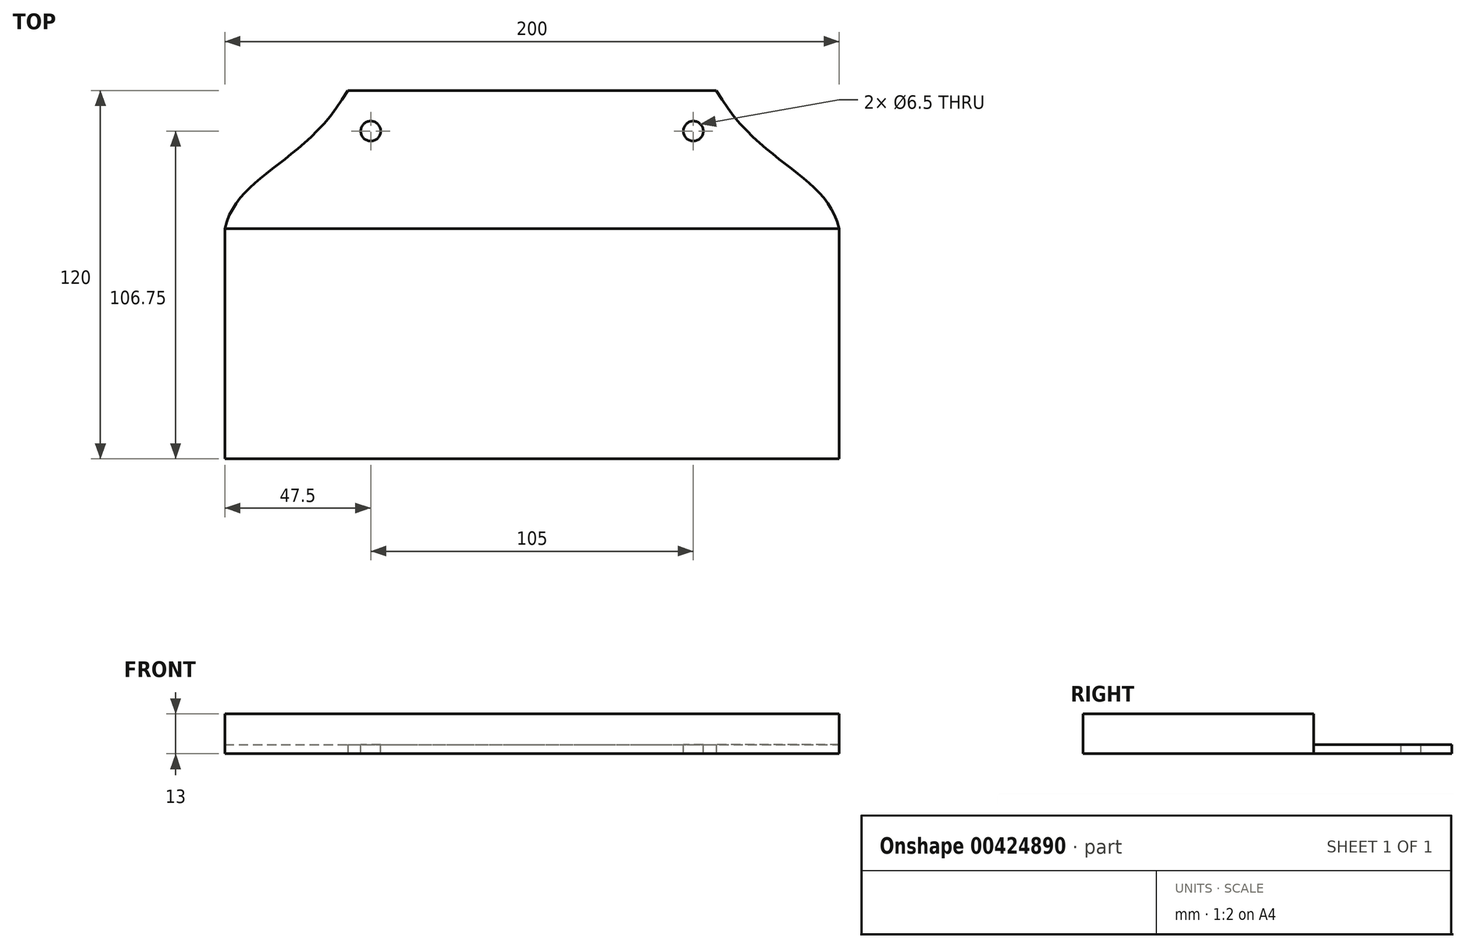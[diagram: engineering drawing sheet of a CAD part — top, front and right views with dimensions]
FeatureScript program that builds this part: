
annotation { "Feature Type Name" : "Feature", "Feature Type Description" : "" }
export const myFeature = defineFeature(function(context is Context, id is Id, definition is map)
    precondition{}
    {
        {
            var Q0;
            Q0=qCreatedBy(makeId("Top.planeOp"),FACE);
            var sketch = newSketch(context, id + "F0", { "sketchPlane" : qUnion([Q0])});
            skLineSegment(sketch, "E0.bottom", {"start": v(-60, -22.5) * mm, "end": v(60, -22.5) * mm});
            skLineSegment(sketch, "E0.top", {"start": v(-60, 22.5) * mm, "end": v(60, 22.5) * mm});
            skLineSegment(sketch, "E0.left", {"start": v(-60, -22.5) * mm, "end": v(-60, 22.5) * mm});
            skLineSegment(sketch, "E0.right", {"start": v(60, -22.5) * mm, "end": v(60, 22.5) * mm});
            skPoint(sketch, "E0.middle", {"position": v(0, 0) * mm});
            skLineSegment(sketch, "E1.top", {"start": v(-60, -97.5) * mm, "end": v(60, -97.5) * mm});
            skLineSegment(sketch, "E1.left", {"start": v(-60, -22.5) * mm, "end": v(-60, -97.5) * mm});
            skLineSegment(sketch, "E1.right", {"start": v(60, -22.5) * mm, "end": v(60, -97.5) * mm});
            skLineSegment(sketch, "E2.bottom", {"start": v(60, -22.5) * mm, "end": v(100, -22.5) * mm});
            skLineSegment(sketch, "E2.top", {"start": v(60, -97.5) * mm, "end": v(100, -97.5) * mm});
            skLineSegment(sketch, "E2.right", {"start": v(100, -22.5) * mm, "end": v(100, -97.5) * mm});
            skLineSegment(sketch, "E3", {"start": v(0, 0) * mm, "end": v(0, -97.5) * mm, "construction": true});
            skLineSegment(sketch, "E4.MirrorCS", {"start": v(-60, -22.5) * mm, "end": v(-100, -22.5) * mm});
            skLineSegment(sketch, "E5.MirrorCS", {"start": v(-100, -22.5) * mm, "end": v(-100, -97.5) * mm});
            skLineSegment(sketch, "E6.MirrorCS", {"start": v(-60, -97.5) * mm, "end": v(-100, -97.5) * mm});
            skFitSpline(sketch, "E7", {"points": [v(-100, -22.5) * mm, v(-60, 22.5) * mm], "startDerivative": vector(12.96, 54.24) * mm, "endDerivative": vector(40.87, 72.11) * mm});
            skFitSpline(sketch, "E8.MirrorCS", {"points": [v(100, -22.5) * mm, v(60, 22.5) * mm], "startDerivative": vector(-12.96, 54.24) * mm, "endDerivative": vector(-40.87, 72.11) * mm});
            skSolve(sketch);
        }
        {
            var Q0;
            Q0 = qSketchRegion(id + "F0", true);
            extrude(context, id + "F1", {"entities" : qUnion([Q0]), "depth" : 3 * mm});
        }
        {
            var Q0;
            Q0=makeQuery(id+"F1.opExtrude","CAP_FACE",FACE,{"disambiguationData":[OSD([sQuery(id+"F0.wireOp",EDGE,"E0.top"),sQuery(id+"F0.wireOp",EDGE,"E1.top"),sQuery(id+"F0.wireOp",EDGE,"E2.top"),sQuery(id+"F0.wireOp",EDGE,"E2.right"),sQuery(id+"F0.wireOp",EDGE,"E5.MirrorCS"),sQuery(id+"F0.wireOp",EDGE,"E6.MirrorCS"),sQuery(id+"F0.wireOp",EDGE,"E7"),sQuery(id+"F0.wireOp",EDGE,"E8.MirrorCS")])],"isStart":false});
            var sketch = newSketch(context, id + "F2", { "sketchPlane" : qUnion([Q0])});
            skLineSegment(sketch, "E9.0.1", {"start": v(-100, -22.5) * mm, "end": v(-100, -97.5) * mm});
            skLineSegment(sketch, "E9.0.2", {"start": v(-100, -97.5) * mm, "end": v(100, -97.5) * mm});
            skLineSegment(sketch, "E9.0.3", {"start": v(100, -97.5) * mm, "end": v(100, -22.5) * mm});
            skLineSegment(sketch, "E10", {"start": v(-100, -22.5) * mm, "end": v(100, -22.5) * mm});
            skPoint(sketch, "E9.0.5.end.orphan", {"position": v(-60, 22.5) * mm});
            skPoint(sketch, "E9.0.4.end.orphan", {"position": v(60, 22.5) * mm});
            skSolve(sketch);
        }
        {
            var Q0;
            Q0 = qSketchRegion(id + "F2", true);
            extrude(context, id + "F3", {"entities" : qUnion([Q0]), "operationType" : NewBodyOperationType.ADD, "depth" : 10 * mm});
        }
        {
            var Q0;
            Q0=makeQuery(id+"F1.opExtrude","CAP_FACE",FACE,{"disambiguationData":[OSD([sQuery(id+"F0.wireOp",EDGE,"E0.top"),sQuery(id+"F0.wireOp",EDGE,"E1.top"),sQuery(id+"F0.wireOp",EDGE,"E2.top"),sQuery(id+"F0.wireOp",EDGE,"E2.right"),sQuery(id+"F0.wireOp",EDGE,"E5.MirrorCS"),sQuery(id+"F0.wireOp",EDGE,"E6.MirrorCS"),sQuery(id+"F0.wireOp",EDGE,"E7"),sQuery(id+"F0.wireOp",EDGE,"E8.MirrorCS")])],"isStart":false});
            var sketch = newSketch(context, id + "F4", { "sketchPlane" : qUnion([Q0])});
            skLineSegment(sketch, "E11", {"start": v(0, 22.5) * mm, "end": v(0, -22.5) * mm, "construction": true});
            skCircle(sketch, "E12", {"center": v(-52.5, 9.25) * mm, "radius": 3.25 * mm});
            skCircle(sketch, "E13.MirrorC", {"center": v(52.5, 9.25) * mm, "radius": 3.25 * mm});
            skSolve(sketch);
        }
        {
            var Q0;
            Q0 = qSketchRegion(id + "F4", true);
            extrude(context, id + "F5", {"entities" : qUnion([Q0]), "operationType" : NewBodyOperationType.REMOVE, "oppositeDirection" : true, "depth" : 25 * mm});
        }
    });
